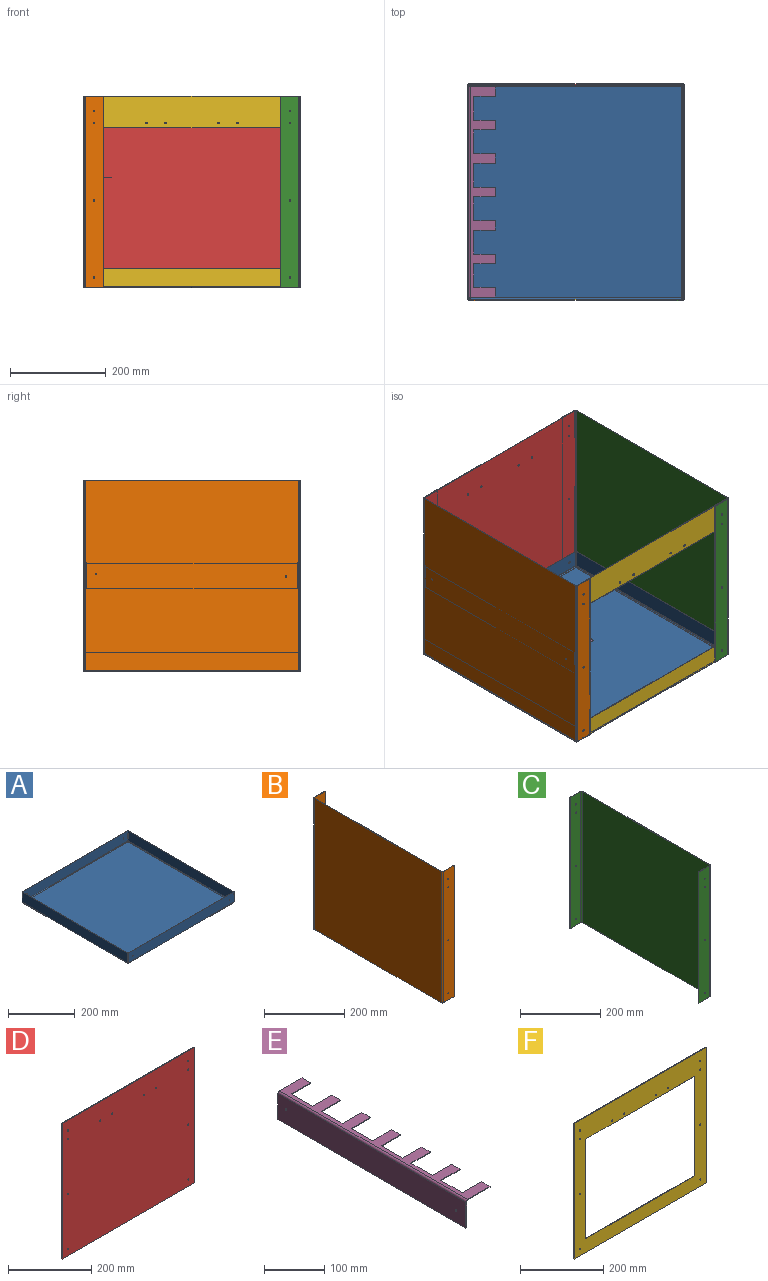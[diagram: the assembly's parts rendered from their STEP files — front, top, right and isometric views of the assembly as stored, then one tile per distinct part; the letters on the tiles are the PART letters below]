
ASSEMBLY  parts=6 mates=5
PART A: 50 faces, bbox 450x450x40 mm
  f0: plane 442.62x442.62mm, normal (0,0,-1), area 195912.5mm2, adj f13,f26,f37,f48
  f1: plane 442.62x442.62mm, normal (0,0,1), area 195912.5mm2, adj f14,f27,f38,f49
  f2: plane 2.48x1.19mm, normal (0,0,-1), area 3mm2, adj f4,f9,f10,f12
  f3: plane 447.58x1.19mm, normal (0,0,1), area 532.6mm2, adj f4,f8,f9,f10
  f4: plane 36.31x1.19mm, normal (1,0,0), area 43.2mm2, adj f2,f3,f9,f10
  f5: plane 2.48x1.19mm, normal (0,0,-1), area 3mm2, adj f8,f9,f10,f11
  f6: cylinder r=1.75mm len=3.5mm, axis (0,1,0), area 13.1mm2, adj f9,f10
  f7: cylinder r=1.75mm len=3.5mm, axis (0,1,0), area 13.1mm2, adj f9,f10
  f8: plane 36.31x1.19mm, normal (-1,0,0), area 43.2mm2, adj f3,f5,f9,f10
  f9: plane 447.58x36.31mm, normal (0,1,0), area 16232.4mm2, adj f2,f3,f4,f5,f6,f7,f8,f13
  f10: plane 447.58x36.31mm, normal (0,-1,0), area 16232.4mm2, adj f2,f3,f4,f5,f6,f7,f8,f14
  f11: plane 3.69x3.69mm, normal (-1,0,0), area 5.8mm2, adj f5,f13,f14,f47
  f12: plane 3.69x3.69mm, normal (1,0,0), area 5.8mm2, adj f2,f13,f14,f35
  f13: cylinder r=3.69mm len=442.62mm, axis (-1,0,0), area 2565.5mm2, adj f0,f9,f11,f12
  f14: cylinder r=2.5mm len=442.62mm, axis (-1,0,0), area 1738.2mm2, adj f1,f10,f11,f12
  f15: plane 2.48x1.19mm, normal (0,0,-1), area 3mm2, adj f17,f22,f23,f25
  f16: plane 447.58x1.19mm, normal (0,0,1), area 532.6mm2, adj f17,f21,f22,f23
  f17: plane 36.31x1.19mm, normal (-1,0,0), area 43.2mm2, adj f15,f16,f22,f23
  f18: plane 2.48x1.19mm, normal (0,0,-1), area 3mm2, adj f21,f22,f23,f24
  f19: cylinder r=1.75mm len=3.5mm, axis (0,-1,0), area 13.1mm2, adj f22,f23
  f20: cylinder r=1.75mm len=3.5mm, axis (0,-1,0), area 13.1mm2, adj f22,f23
  f21: plane 36.31x1.19mm, normal (1,0,0), area 43.2mm2, adj f16,f18,f22,f23
  f22: plane 447.58x36.31mm, normal (0,-1,0), area 16232.4mm2, adj f15,f16,f17,f18,f19,f20,f21,f26
  f23: plane 447.58x36.31mm, normal (0,1,0), area 16232.4mm2, adj f15,f16,f17,f18,f19,f20,f21,f27
  f24: plane 3.69x3.69mm, normal (1,0,0), area 5.8mm2, adj f18,f26,f27,f36
  f25: plane 3.69x3.69mm, normal (-1,0,0), area 5.8mm2, adj f15,f26,f27,f46
  f26: cylinder r=3.69mm len=442.62mm, axis (1,0,0), area 2565.5mm2, adj f0,f22,f24,f25
  f27: cylinder r=2.5mm len=442.62mm, axis (1,0,0), area 1738.2mm2, adj f1,f23,f24,f25
  f28: plane 2.48x1.19mm, normal (0,0,-1), area 3mm2, adj f30,f33,f34,f36
  f29: plane 447.58x1.19mm, normal (0,0,1), area 532.6mm2, adj f30,f32,f33,f34
  f30: plane 36.31x1.19mm, normal (0,-1,0), area 43.2mm2, adj f28,f29,f33,f34
  f31: plane 2.48x1.19mm, normal (0,0,-1), area 3mm2, adj f32,f33,f34,f35
  f32: plane 36.31x1.19mm, normal (0,1,0), area 43.2mm2, adj f29,f31,f33,f34
  f33: plane 447.58x36.31mm, normal (1,0,0), area 16251.6mm2, adj f28,f29,f30,f31,f32,f37
  f34: plane 447.58x36.31mm, normal (-1,0,0), area 16251.6mm2, adj f28,f29,f30,f31,f32,f38
  f35: plane 3.69x3.69mm, normal (0,1,0), area 5.8mm2, adj f12,f31,f37,f38
  f36: plane 3.69x3.69mm, normal (0,-1,0), area 5.8mm2, adj f24,f28,f37,f38
  f37: cylinder r=3.69mm len=442.62mm, axis (0,1,0), area 2565.5mm2, adj f0,f33,f35,f36
  f38: cylinder r=2.5mm len=442.62mm, axis (0,1,0), area 1738.2mm2, adj f1,f34,f35,f36
  f39: plane 2.48x1.19mm, normal (0,0,-1), area 3mm2, adj f41,f44,f45,f47
  f40: plane 447.58x1.19mm, normal (0,0,1), area 532.6mm2, adj f41,f43,f44,f45
  f41: plane 36.31x1.19mm, normal (0,1,0), area 43.2mm2, adj f39,f40,f44,f45
  f42: plane 2.48x1.19mm, normal (0,0,-1), area 3mm2, adj f43,f44,f45,f46
  f43: plane 36.31x1.19mm, normal (0,-1,0), area 43.2mm2, adj f40,f42,f44,f45
  f44: plane 447.58x36.31mm, normal (-1,0,0), area 16251.6mm2, adj f39,f40,f41,f42,f43,f48
  f45: plane 447.58x36.31mm, normal (1,0,0), area 16251.6mm2, adj f39,f40,f41,f42,f43,f49
  f46: plane 3.69x3.69mm, normal (0,-1,0), area 5.8mm2, adj f25,f42,f48,f49
  f47: plane 3.69x3.69mm, normal (0,1,0), area 5.8mm2, adj f11,f39,f48,f49
  f48: cylinder r=3.69mm len=442.62mm, axis (0,-1,0), area 2565.5mm2, adj f0,f44,f46,f47
  f49: cylinder r=2.5mm len=442.62mm, axis (0,-1,0), area 1738.2mm2, adj f1,f45,f46,f47
PART B: 30 faces, bbox 41.2x454.8x400 mm
  f0: plane 447.38x1.19mm, normal (0,0,-1), area 532.4mm2, adj f2,f3,f14,f27
  f1: plane 447.38x1.19mm, normal (0,0,1), area 532.4mm2, adj f2,f3,f13,f26
  f2: plane 447.38x400mm, normal (-1,0,0), area 178952mm2, adj f0,f1,f15,f28
  f3: plane 447.38x400mm, normal (1,0,0), area 178952mm2, adj f0,f1,f16,f29
  f4: plane 37.5x1.19mm, normal (0,0,-1), area 44.6mm2, adj f5,f11,f12,f14
  f5: plane 400x1.19mm, normal (1,0,0), area 476mm2, adj f4,f10,f11,f12
  f6: cylinder r=1.75mm len=3.5mm, axis (0,-1,0), area 13.1mm2, adj f11,f12
  f7: cylinder r=1.75mm len=3.5mm, axis (0,-1,0), area 13.1mm2, adj f11,f12
  f8: cylinder r=1.75mm len=3.5mm, axis (0,-1,0), area 13.1mm2, adj f11,f12
  f9: cylinder r=1.75mm len=3.5mm, axis (0,-1,0), area 13.1mm2, adj f11,f12
  f10: plane 37.5x1.19mm, normal (0,0,1), area 44.6mm2, adj f5,f11,f12,f13
  f11: plane 400x37.5mm, normal (0,-1,0), area 14961.5mm2, adj f4,f5,f6,f7,f8,f9,f10,f15
  f12: plane 400x37.5mm, normal (0,1,0), area 14961.5mm2, adj f4,f5,f6,f7,f8,f9,f10,f16
  f13: plane 3.69x3.69mm, normal (0,0,1), area 5.8mm2, adj f1,f10,f15,f16
  f14: plane 3.69x3.69mm, normal (0,0,-1), area 5.8mm2, adj f0,f4,f15,f16
  f15: cylinder r=3.69mm len=400mm, axis (0,0,1), area 2318.5mm2, adj f2,f11,f13,f14
  f16: cylinder r=2.5mm len=400mm, axis (0,0,1), area 1570.8mm2, adj f3,f12,f13,f14
  f17: plane 400x1.19mm, normal (1,0,0), area 476mm2, adj f18,f23,f24,f25
  f18: plane 37.5x1.19mm, normal (0,0,-1), area 44.6mm2, adj f17,f24,f25,f27
  f19: cylinder r=1.75mm len=3.5mm, axis (0,1,0), area 13.1mm2, adj f24,f25
  f20: cylinder r=1.75mm len=3.5mm, axis (0,1,0), area 13.1mm2, adj f24,f25
  f21: cylinder r=1.75mm len=3.5mm, axis (0,1,0), area 13.1mm2, adj f24,f25
  f22: cylinder r=1.75mm len=3.5mm, axis (0,1,0), area 13.1mm2, adj f24,f25
  f23: plane 37.5x1.19mm, normal (0,0,1), area 44.6mm2, adj f17,f24,f25,f26
  f24: plane 400x37.5mm, normal (0,1,0), area 14961.5mm2, adj f17,f18,f19,f20,f21,f22,f23,f28
  f25: plane 400x37.5mm, normal (0,-1,0), area 14961.5mm2, adj f17,f18,f19,f20,f21,f22,f23,f29
  f26: plane 3.69x3.69mm, normal (0,0,1), area 5.8mm2, adj f1,f23,f28,f29
  f27: plane 3.69x3.69mm, normal (0,0,-1), area 5.8mm2, adj f0,f18,f28,f29
  f28: cylinder r=3.69mm len=400mm, axis (0,0,1), area 2318.5mm2, adj f2,f24,f26,f27
  f29: cylinder r=2.5mm len=400mm, axis (0,0,1), area 1570.8mm2, adj f3,f25,f26,f27
PART C: 30 faces, bbox 41.2x454.8x400 mm
  f0: plane 447.38x1.19mm, normal (0,0,1), area 532.4mm2, adj f2,f3,f13,f26
  f1: plane 447.38x1.19mm, normal (0,0,-1), area 532.4mm2, adj f2,f3,f14,f27
  f2: plane 447.38x400mm, normal (1,0,0), area 178952mm2, adj f0,f1,f15,f28
  f3: plane 447.38x400mm, normal (-1,0,0), area 178952mm2, adj f0,f1,f16,f29
  f4: plane 37.5x1.19mm, normal (0,0,1), area 44.6mm2, adj f5,f11,f12,f13
  f5: plane 400x1.19mm, normal (-1,0,0), area 476mm2, adj f4,f10,f11,f12
  f6: cylinder r=1.75mm len=3.5mm, axis (0,-1,0), area 13.1mm2, adj f11,f12
  f7: cylinder r=1.75mm len=3.5mm, axis (0,-1,0), area 13.1mm2, adj f11,f12
  f8: cylinder r=1.75mm len=3.5mm, axis (0,-1,0), area 13.1mm2, adj f11,f12
  f9: cylinder r=1.75mm len=3.5mm, axis (0,-1,0), area 13.1mm2, adj f11,f12
  f10: plane 37.5x1.19mm, normal (0,0,-1), area 44.6mm2, adj f5,f11,f12,f14
  f11: plane 400x37.5mm, normal (0,-1,0), area 14961.5mm2, adj f4,f5,f6,f7,f8,f9,f10,f15
  f12: plane 400x37.5mm, normal (0,1,0), area 14961.5mm2, adj f4,f5,f6,f7,f8,f9,f10,f16
  f13: plane 3.69x3.69mm, normal (0,0,1), area 5.8mm2, adj f0,f4,f15,f16
  f14: plane 3.69x3.69mm, normal (0,0,-1), area 5.8mm2, adj f1,f10,f15,f16
  f15: cylinder r=3.69mm len=400mm, axis (0,0,1), area 2318.5mm2, adj f2,f11,f13,f14
  f16: cylinder r=2.5mm len=400mm, axis (0,0,1), area 1570.8mm2, adj f3,f12,f13,f14
  f17: plane 400x1.19mm, normal (-1,0,0), area 476mm2, adj f18,f23,f24,f25
  f18: plane 37.5x1.19mm, normal (0,0,1), area 44.6mm2, adj f17,f24,f25,f26
  f19: cylinder r=1.75mm len=3.5mm, axis (0,1,0), area 13.1mm2, adj f24,f25
  f20: cylinder r=1.75mm len=3.5mm, axis (0,1,0), area 13.1mm2, adj f24,f25
  f21: cylinder r=1.75mm len=3.5mm, axis (0,1,0), area 13.1mm2, adj f24,f25
  f22: cylinder r=1.75mm len=3.5mm, axis (0,1,0), area 13.1mm2, adj f24,f25
  f23: plane 37.5x1.19mm, normal (0,0,-1), area 44.6mm2, adj f17,f24,f25,f27
  f24: plane 400x37.5mm, normal (0,1,0), area 14961.5mm2, adj f17,f18,f19,f20,f21,f22,f23,f28
  f25: plane 400x37.5mm, normal (0,-1,0), area 14961.5mm2, adj f17,f18,f19,f20,f21,f22,f23,f29
  f26: plane 3.69x3.69mm, normal (0,0,1), area 5.8mm2, adj f0,f18,f28,f29
  f27: plane 3.69x3.69mm, normal (0,0,-1), area 5.8mm2, adj f1,f23,f28,f29
  f28: cylinder r=3.69mm len=400mm, axis (0,0,1), area 2318.5mm2, adj f2,f24,f26,f27
  f29: cylinder r=2.5mm len=400mm, axis (0,0,1), area 1570.8mm2, adj f3,f25,f26,f27
PART D: 18 faces, bbox 450x1.2x400 mm
  f0: plane 450x1.19mm, normal (0,0,1), area 535.5mm2, adj f1,f15,f16,f17
  f1: plane 400x1.19mm, normal (1,0,0), area 476mm2, adj f0,f2,f16,f17
  f2: plane 450x1.19mm, normal (0,0,-1), area 535.5mm2, adj f1,f15,f16,f17
  f3: cylinder r=1.75mm len=3.5mm, axis (0,-1,0), area 13.1mm2, adj f16,f17
  f4: cylinder r=1.75mm len=3.5mm, axis (0,-1,0), area 13.1mm2, adj f16,f17
  f5: cylinder r=1.75mm len=3.5mm, axis (0,-1,0), area 13.1mm2, adj f16,f17
  f6: cylinder r=1.75mm len=3.5mm, axis (0,-1,0), area 13.1mm2, adj f16,f17
  f7: cylinder r=1.75mm len=3.5mm, axis (0,-1,0), area 13.1mm2, adj f16,f17
  f8: cylinder r=1.75mm len=3.5mm, axis (0,-1,0), area 13.1mm2, adj f16,f17
  f9: cylinder r=1.75mm len=3.5mm, axis (0,-1,0), area 13.1mm2, adj f16,f17
  f10: cylinder r=1.75mm len=3.5mm, axis (0,-1,0), area 13.1mm2, adj f16,f17
  f11: cylinder r=1.75mm len=3.5mm, axis (0,-1,0), area 13.1mm2, adj f16,f17
  f12: cylinder r=1.75mm len=3.5mm, axis (0,-1,0), area 13.1mm2, adj f16,f17
  f13: cylinder r=1.75mm len=3.5mm, axis (0,-1,0), area 13.1mm2, adj f16,f17
  f14: cylinder r=1.75mm len=3.5mm, axis (0,-1,0), area 13.1mm2, adj f16,f17
  f15: plane 400x1.19mm, normal (-1,0,0), area 476mm2, adj f0,f2,f16,f17
  f16: plane 450x400mm, normal (0,1,0), area 179884.5mm2, adj f0,f1,f2,f3,f4,f5,f6,f7
  f17: plane 450x400mm, normal (0,-1,0), area 179884.5mm2, adj f0,f1,f2,f3,f4,f5,f6,f7
PART E: 40 faces, bbox 56.2x440x56.2 mm
  f0: plane 52.5x1.19mm, normal (0,1,0), area 62.5mm2, adj f1,f3,f4,f35
  f1: plane 440x1.19mm, normal (0,0,-1), area 523.6mm2, adj f0,f2,f3,f4
  f2: plane 52.5x1.19mm, normal (0,-1,0), area 62.5mm2, adj f1,f3,f4,f34
  f3: plane 440x52.5mm, normal (-1,0,0), area 23081.8mm2, adj f0,f1,f2,f36,f38,f39
  f4: plane 440x52.5mm, normal (1,0,0), area 23081.8mm2, adj f0,f1,f2,f37,f38,f39
  f5: plane 52.5x1.19mm, normal (0,-1,0), area 62.5mm2, adj f6,f32,f33,f34
  f6: plane 20x1.19mm, normal (1,0,0), area 23.8mm2, adj f5,f7,f32,f33
  f7: plane 45.09x1.19mm, normal (0,1,0), area 53.7mm2, adj f6,f8,f32,f33
  f8: plane 50x1.19mm, normal (1,0,0), area 59.5mm2, adj f7,f9,f32,f33
  f9: plane 45.09x1.19mm, normal (0,-1,0), area 53.7mm2, adj f8,f10,f32,f33
  f10: plane 20x1.19mm, normal (1,0,0), area 23.8mm2, adj f9,f11,f32,f33
  f11: plane 45.09x1.19mm, normal (0,1,0), area 53.7mm2, adj f10,f12,f32,f33
  f12: plane 50x1.19mm, normal (1,0,0), area 59.5mm2, adj f11,f13,f32,f33
  f13: plane 45.09x1.19mm, normal (0,-1,0), area 53.7mm2, adj f12,f14,f32,f33
  f14: plane 20x1.19mm, normal (1,0,0), area 23.8mm2, adj f13,f15,f32,f33
  f15: plane 45.09x1.19mm, normal (0,1,0), area 53.7mm2, adj f14,f16,f32,f33
  f16: plane 50x1.19mm, normal (1,0,0), area 59.5mm2, adj f15,f17,f32,f33
  f17: plane 45.09x1.19mm, normal (0,-1,0), area 53.7mm2, adj f16,f18,f32,f33
  f18: plane 20x1.19mm, normal (1,0,0), area 23.8mm2, adj f17,f19,f32,f33
  f19: plane 45.09x1.19mm, normal (0,1,0), area 53.7mm2, adj f18,f20,f32,f33
  f20: plane 50x1.19mm, normal (1,0,0), area 59.5mm2, adj f19,f21,f32,f33
  f21: plane 45.09x1.19mm, normal (0,-1,0), area 53.7mm2, adj f20,f22,f32,f33
  f22: plane 20x1.19mm, normal (1,0,0), area 23.8mm2, adj f21,f23,f32,f33
  f23: plane 45.09x1.19mm, normal (0,1,0), area 53.7mm2, adj f22,f24,f32,f33
  f24: plane 50x1.19mm, normal (1,0,0), area 59.5mm2, adj f23,f25,f32,f33
  f25: plane 45.09x1.19mm, normal (0,-1,0), area 53.7mm2, adj f24,f26,f32,f33
  f26: plane 20x1.19mm, normal (1,0,0), area 23.8mm2, adj f25,f27,f32,f33
  f27: plane 45.09x1.19mm, normal (0,1,0), area 53.7mm2, adj f26,f28,f32,f33
  f28: plane 50x1.19mm, normal (1,0,0), area 59.5mm2, adj f27,f29,f32,f33
  f29: plane 45.09x1.19mm, normal (0,-1,0), area 53.7mm2, adj f28,f30,f32,f33
  f30: plane 20x1.19mm, normal (1,0,0), area 23.8mm2, adj f29,f31,f32,f33
  f31: plane 52.5x1.19mm, normal (0,1,0), area 62.5mm2, adj f30,f32,f33,f35
  f32: plane 440x52.5mm, normal (0,0,1), area 9571.9mm2, adj f5,f6,f7,f8,f9,f10,f11,f12
  f33: plane 440x52.5mm, normal (0,0,-1), area 9571.9mm2, adj f5,f6,f7,f8,f9,f10,f11,f12
  f34: plane 3.69x3.69mm, normal (0,-1,0), area 5.8mm2, adj f2,f5,f36,f37
  f35: plane 3.69x3.69mm, normal (0,1,0), area 5.8mm2, adj f0,f31,f36,f37
  f36: cylinder r=3.69mm len=440mm, axis (0,-1,0), area 2550.3mm2, adj f3,f32,f34,f35
  f37: cylinder r=2.5mm len=440mm, axis (0,-1,0), area 1727.9mm2, adj f4,f33,f34,f35
  f38: cylinder r=1.7mm len=3.4mm, axis (-1,0,0), area 12.7mm2, adj f3,f4
  f39: cylinder r=1.7mm len=3.4mm, axis (-1,0,0), area 12.7mm2, adj f3,f4
PART F: 22 faces, bbox 450x1.2x400 mm
  f0: plane 450x1.19mm, normal (0,0,1), area 535.5mm2, adj f1,f19,f20,f21
  f1: plane 400x1.19mm, normal (-1,0,0), area 476mm2, adj f0,f2,f20,f21
  f2: plane 450x1.19mm, normal (0,0,-1), area 535.5mm2, adj f1,f19,f20,f21
  f3: plane 294x1.19mm, normal (1,0,0), area 349.9mm2, adj f4,f18,f20,f21
  f4: plane 370x1.19mm, normal (0,0,-1), area 440.3mm2, adj f3,f5,f20,f21
  f5: plane 294x1.19mm, normal (-1,0,0), area 349.9mm2, adj f4,f18,f20,f21
  f6: cylinder r=1.75mm len=3.5mm, axis (0,-1,0), area 13.1mm2, adj f20,f21
  f7: cylinder r=1.75mm len=3.5mm, axis (0,-1,0), area 13.1mm2, adj f20,f21
  f8: cylinder r=1.75mm len=3.5mm, axis (0,-1,0), area 13.1mm2, adj f20,f21
  f9: cylinder r=1.75mm len=3.5mm, axis (0,-1,0), area 13.1mm2, adj f20,f21
  f10: cylinder r=1.75mm len=3.5mm, axis (0,-1,0), area 13.1mm2, adj f20,f21
  f11: cylinder r=1.75mm len=3.5mm, axis (0,-1,0), area 13.1mm2, adj f20,f21
  f12: cylinder r=1.75mm len=3.5mm, axis (0,-1,0), area 13.1mm2, adj f20,f21
  f13: cylinder r=1.75mm len=3.5mm, axis (0,-1,0), area 13.1mm2, adj f20,f21
  f14: cylinder r=1.75mm len=3.5mm, axis (0,-1,0), area 13.1mm2, adj f20,f21
  f15: cylinder r=1.75mm len=3.5mm, axis (0,-1,0), area 13.1mm2, adj f20,f21
  f16: cylinder r=1.75mm len=3.5mm, axis (0,-1,0), area 13.1mm2, adj f20,f21
  f17: cylinder r=1.75mm len=3.5mm, axis (0,-1,0), area 13.1mm2, adj f20,f21
  f18: plane 370x1.19mm, normal (0,0,1), area 440.3mm2, adj f3,f5,f20,f21
  f19: plane 400x1.19mm, normal (1,0,0), area 476mm2, adj f0,f2,f20,f21
  f20: plane 450x400mm, normal (0,-1,0), area 71104.5mm2, adj f0,f1,f2,f3,f4,f5,f6,f7
  f21: plane 450x400mm, normal (0,1,0), area 71104.5mm2, adj f0,f1,f2,f3,f4,f5,f6,f7
PLACE A at identity fixed
PLACE B at identity
PLACE C at identity
PLACE D at identity
PLACE E t=(-218.9,0,230.22)mm
PLACE F at identity
MATE fastened D.f4 <-> A.f7  axis (0,-1,0) through (-205,225,20)mm
MATE fastened E.f3 <-> B.f3  axis (-1,0,0) through (-225,0,200)mm
MATE fastened B.f6 <-> D.f4  axis (0,-1,0) through (-205,226.19,20)mm
MATE fastened F.f7 <-> A.f20  axis (0,1,0) through (-205,-225,20)mm
MATE fastened C.f7 <-> D.f5  axis (0,-1,0) through (205,226.19,20)mm
